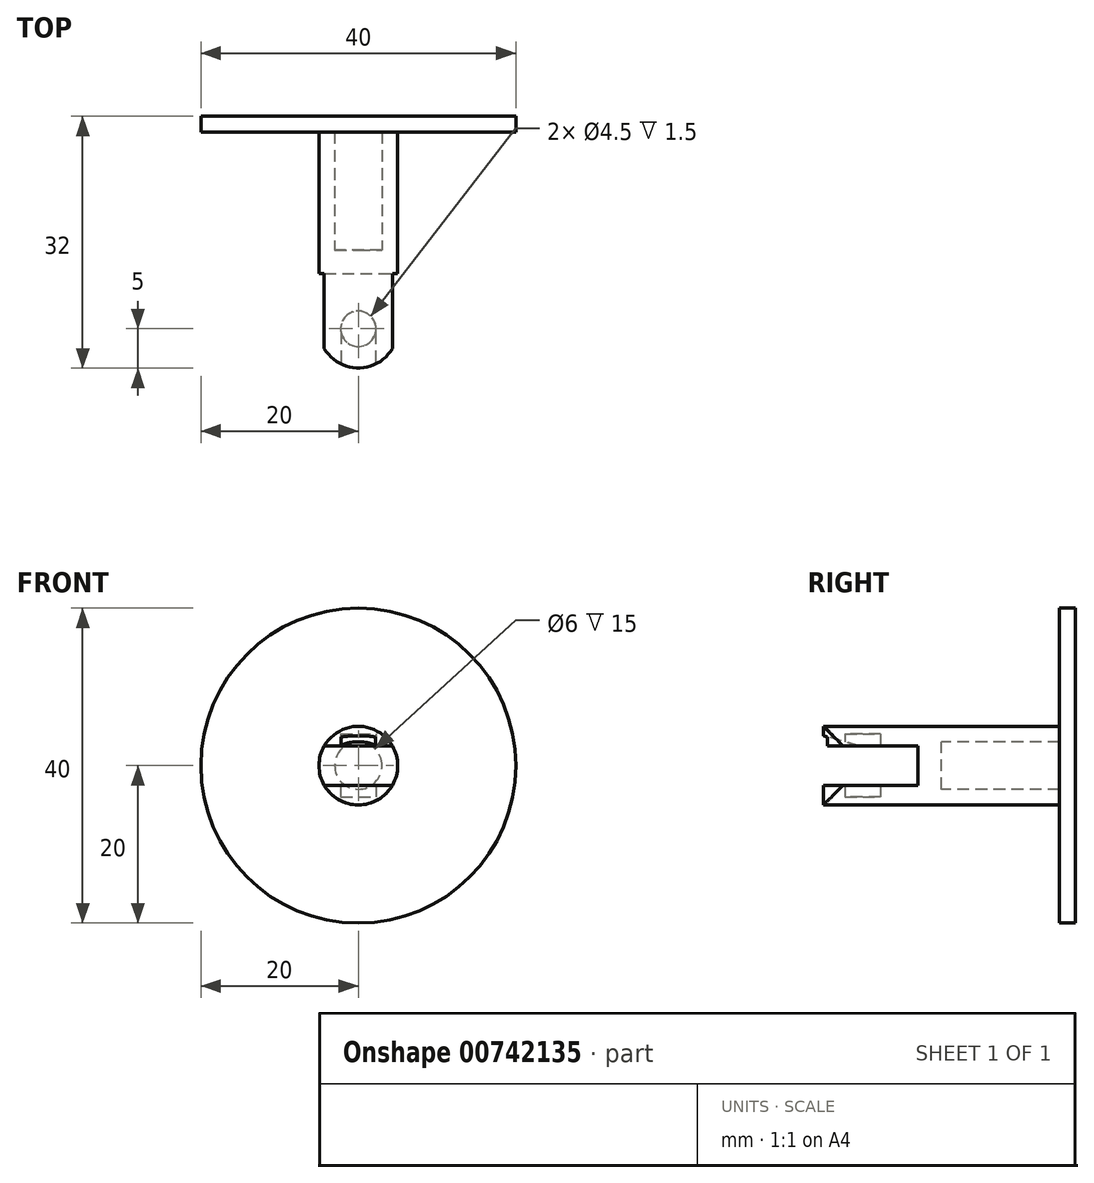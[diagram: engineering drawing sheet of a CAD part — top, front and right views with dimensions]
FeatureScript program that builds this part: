
annotation { "Feature Type Name" : "Feature", "Feature Type Description" : "" }
export const myFeature = defineFeature(function(context is Context, id is Id, definition is map)
    precondition{}
    {
        {
            var Q0;
            Q0=qCreatedBy(makeId("Front.planeOp"),FACE);
            var sketch = newSketch(context, id + "F0", { "sketchPlane" : qUnion([Q0])});
            skCircle(sketch, "E0", {"center": v(0, 0) * mm, "radius": 20 * mm});
            skSolve(sketch);
        }
        {
            var Q0;
            Q0=makeQuery(id+"F0.imprint","IMPRINT",FACE,{"disambiguationData":[TD([[makeQuery(id+"F0.imprint","IMPRINT",EDGE,{"derivedFrom":sQuery(id+"F0.wireOp",EDGE,"E0")}),1.0]])]});
            extrude(context, id + "F1", {"entities" : qUnion([Q0]), "depth" : 2 * mm, "offsetDistance" : 25 * mm});
        }
        {
            var Q0;
            Q0=makeQuery(id+"F1.opExtrude","CAP_FACE",FACE,{"disambiguationData":[OSD([sQuery(id+"F0.wireOp",EDGE,"E0")])],"isStart":false});
            var sketch = newSketch(context, id + "F2", { "sketchPlane" : qUnion([Q0])});
            skCircle(sketch, "E1", {"center": v(0, 0) * mm, "radius": 5 * mm});
            skSolve(sketch);
        }
        {
            var Q0;
            Q0 = qSketchRegion(id + "F2", true);
            extrude(context, id + "F3", {"entities" : qUnion([Q0]), "operationType" : NewBodyOperationType.ADD, "depth" : 30 * mm, "offsetDistance" : 25 * mm});
        }
        {
            var Q0;
            Q0=makeQuery(id+"F3.opExtrude","CAP_FACE",FACE,{"disambiguationData":[OSD([sQuery(id+"F2.wireOp",EDGE,"E1")])],"isStart":false});
            var sketch = newSketch(context, id + "F4", { "sketchPlane" : qUnion([Q0])});
            skSolve(sketch);
        }
        {
            var Q0;
            Q0=makeQuery(id+"F4.imprint","IMPRINT",FACE,{"disambiguationData":[TD([[makeQuery(id+"F4.imprint","IMPRINT",EDGE,{"derivedFrom":makeQuery(id+"F3.opExtrude","CAP_EDGE",EDGE,{"disambiguationData":[OSD([sQuery(id+"F2.wireOp",EDGE,"E1")])],"isStart":false})}),1.0]])]});
            var sketch = newSketch(context, id + "F5", { "sketchPlane" : qUnion([Q0])});
            skLineSegment(sketch, "E2.bottom", {"start": v(-5, 2.5) * mm, "end": v(5, 2.5) * mm});
            skLineSegment(sketch, "E2.top", {"start": v(-5, -2.5) * mm, "end": v(5, -2.5) * mm});
            skLineSegment(sketch, "E2.left", {"start": v(-5, 2.5) * mm, "end": v(-5, -2.5) * mm});
            skLineSegment(sketch, "E2.right", {"start": v(5, 2.5) * mm, "end": v(5, -2.5) * mm});
            skCircle(sketch, "E3.0", {"center": v(0, 0) * mm, "radius": 5 * mm});
            skSolve(sketch);
        }
        {
            var Q0;
            {var subQ0=sQuery(id+"F5.wireOp",EDGE,"E3.0");var subQ1=sQuery(id+"F5.wireOp",EDGE,"E2.bottom");var subQ2=makeQuery(id+"F5.imprint","INTERSECT",VERTEX,{"disambiguationData":[OD(0.0)],"derivedFrom":[subQ1,subQ0]});Q0=makeQuery(id+"F5.imprint","IMPRINT",FACE,{"disambiguationData":[TD([[makeQuery(id+"F5.imprint","IMPRINT",EDGE,{"disambiguationData":[TD([[subQ2,-1.0]])],"derivedFrom":subQ1}),-1.0]])]});}
            extrude(context, id + "F6", {"entities" : qUnion([Q0]), "operationType" : NewBodyOperationType.REMOVE, "oppositeDirection" : true, "depth" : 12 * mm, "offsetDistance" : 25 * mm});
        }
        {
            var Q0;
            Q0=makeQuery(id+"F6.boolean.opBoolean","COPY",FACE,{"derivedFrom":makeQuery(id+"F6.opExtrude","SWEPT_FACE",FACE,{"disambiguationData":[OSD([sQuery(id+"F5.wireOp",EDGE,"E2.bottom")])]})});
            var sketch = newSketch(context, id + "F7", { "sketchPlane" : qUnion([Q0])});
            skCircle(sketch, "E4", {"center": v(0, 27) * mm, "radius": 2.25 * mm});
            skSolve(sketch);
        }
        {
            var Q0;
            Q0 = qSketchRegion(id + "F7", true);
            extrude(context, id + "F8", {"entities" : qUnion([Q0]), "operationType" : NewBodyOperationType.REMOVE, "oppositeDirection" : true, "depth" : 1.5 * mm, "offsetDistance" : 25 * mm, "hasSecondDirection" : true, "secondDirectionOppositeDirection" : false, "secondDirectionDepth" : 6.5 * mm});
        }
        {
            var Q0;
            Q0=makeQuery(id+"F6.boolean.opBoolean","COPY",FACE,{"derivedFrom":makeQuery(id+"F6.opExtrude","SWEPT_FACE",FACE,{"disambiguationData":[OSD([sQuery(id+"F5.wireOp",EDGE,"E2.top")])]})});
            var sketch = newSketch(context, id + "F9", { "sketchPlane" : qUnion([Q0])});
            skCircle(sketch, "E5", {"center": v(0, -27) * mm, "radius": 5 * mm});
            skSolve(sketch);
        }
        {
            var Q0;
            {var subQ0=sQuery(id+"F9.wireOp",EDGE,"E5");var subQ1=sQuery(id+"F5.wireOp",EDGE,"E2.top");var subQ2=makeQuery(id+"F6.boolean.opBoolean","COPY",EDGE,{"derivedFrom":makeQuery(id+"F6.opExtrude","CAP_EDGE",EDGE,{"disambiguationData":[OSD([subQ1])],"isStart":true})});var subQ3=makeQuery(id+"F9.imprint","INTERSECT",VERTEX,{"derivedFrom":[subQ2,subQ0]});Q0=makeQuery(id+"F9.imprint","IMPRINT",FACE,{"disambiguationData":[TD([[makeQuery(id+"F9.imprint","IMPRINT",EDGE,{"disambiguationData":[TD([[subQ3,-1.0]])],"derivedFrom":subQ0}),-1.0]])]});}
            var Q1;
            {var subQ0=sQuery(id+"F9.wireOp",EDGE,"E5");var subQ2=sQuery(id+"F5.wireOp",EDGE,"E2.top");var subQ5=makeQuery(id+"F6.boolean.opBoolean","COPY",EDGE,{"derivedFrom":makeQuery(id+"F6.opExtrude","CAP_EDGE",EDGE,{"disambiguationData":[OSD([subQ2])],"isStart":true})});var subQ6=makeQuery(id+"F9.imprint","INTERSECT",VERTEX,{"derivedFrom":[subQ5,subQ0]});Q1=makeQuery(id+"F9.imprint","IMPRINT",FACE,{"disambiguationData":[TD([[makeQuery(id+"F9.imprint","IMPRINT",EDGE,{"disambiguationData":[TD([[subQ6,1.0]])],"derivedFrom":subQ0}),-1.0]])]});}
            extrude(context, id + "F10", {"entities" : qUnion([Q0, Q1]), "operationType" : NewBodyOperationType.REMOVE, "endBound" : BoundingType.THROUGH_ALL, "oppositeDirection" : true, "depth" : 25 * mm, "offsetDistance" : 25 * mm, "hasSecondDirection" : true, "secondDirectionBound" : SecondDirectionBoundingType.THROUGH_ALL, "secondDirectionOppositeDirection" : false, "secondDirectionDepth" : 25 * mm});
        }
        {
            var Q0;
            Q0=qCreatedBy(makeId("Right.planeOp"),FACE);
            var sketch = newSketch(context, id + "F11", { "sketchPlane" : qUnion([Q0])});
            skLineSegment(sketch, "E6.0.0", {"start": v(-20, 2.5) * mm, "end": v(-29.5, 2.5) * mm});
            skLineSegment(sketch, "E6.0.1", {"start": v(-29.5, 2.5) * mm, "end": v(-32, 2.5) * mm});
            skLineSegment(sketch, "E6.0.2", {"start": v(-29.5, 2.5) * mm, "end": v(-20, 2.5) * mm});
            skLineSegment(sketch, "E7", {"start": v(-32, 2.5) * mm, "end": v(-32, 5) * mm});
            skLineSegment(sketch, "E8", {"start": v(-32, 5) * mm, "end": v(-2, 5) * mm});
            skLineSegment(sketch, "E9.0.0", {"start": v(-29.5, -2.5) * mm, "end": v(-32, -2.5) * mm});
            skLineSegment(sketch, "E9.0.1", {"start": v(-29.5, -2.5) * mm, "end": v(-20, -2.5) * mm});
            skLineSegment(sketch, "E9.0.3", {"start": v(-20, -2.5) * mm, "end": v(-29.5, -2.5) * mm});
            skLineSegment(sketch, "E10", {"start": v(-32, -5) * mm, "end": v(-32, -2.5) * mm});
            skLineSegment(sketch, "E11", {"start": v(-2, -5) * mm, "end": v(-32, -5) * mm});
            skLineSegment(sketch, "E12.0.0", {"start": v(-20, 2.5) * mm, "end": v(-20, -2.5) * mm});
            skLineSegment(sketch, "E12.0.2", {"start": v(-20, -2.5) * mm, "end": v(-20, 2.5) * mm});
            skLineSegment(sketch, "E13.0", {"start": v(-24.75, 4) * mm, "end": v(-29.25, 4) * mm});
            skLineSegment(sketch, "E14", {"start": v(-29.25, 4) * mm, "end": v(-29.5, 2.5) * mm});
            skLineSegment(sketch, "E15", {"start": v(-29.4, 3.06) * mm, "end": v(-32, 3.8) * mm});
            skLineSegment(sketch, "E16", {"start": v(-29.4, 3.06) * mm, "end": v(-27.47, 2.5) * mm});
            skSolve(sketch);
        }
        {
            var Q0;
            {var subQ0=sQuery(id+"F11.wireOp",EDGE,"E6.0.1");Q0=makeQuery(id+"F11.imprint","IMPRINT",FACE,{"disambiguationData":[TD([[makeQuery(id+"F11.imprint","IMPRINT",EDGE,{"derivedFrom":subQ0}),-1.0]])]});}
            var Q1;
            {var subQ3=sQuery(id+"F11.wireOp",EDGE,"E16");Q1=makeQuery(id+"F11.imprint","IMPRINT",FACE,{"disambiguationData":[TD([[makeQuery(id+"F11.imprint","IMPRINT",EDGE,{"derivedFrom":subQ3}),-1.0]])]});}
            extrude(context, id + "F12", {"entities" : qUnion([Q0, Q1]), "operationType" : NewBodyOperationType.REMOVE, "oppositeDirection" : true, "depth" : 2.2 * mm, "offsetDistance" : 25 * mm, "hasSecondDirection" : true, "secondDirectionOppositeDirection" : false, "secondDirectionDepth" : 2.2 * mm});
        }
        {
            var Q0;
            Q0=makeQuery(id+"F6.boolean.opBoolean","COPY",FACE,{"derivedFrom":makeQuery(id+"F6.opExtrude","SWEPT_FACE",FACE,{"disambiguationData":[OSD([sQuery(id+"F5.wireOp",EDGE,"E2.top")])]})});
            var Q1;
            Q1=makeQuery(id+"F6.boolean.opBoolean","COPY",FACE,{"derivedFrom":makeQuery(id+"F6.opExtrude","SWEPT_FACE",FACE,{"disambiguationData":[OSD([sQuery(id+"F5.wireOp",EDGE,"E2.bottom")])]})});
            cPlane(context, id + "F13", {"entities" : qUnion([Q0, Q1]), "cplaneType" : CPlaneType.MID_PLANE, "offset" : 25 * mm, "width" : 150 * mm, "height" : 150 * mm});
        }
        {
            var Q0;
            Q0=makeQuery(id+"F6.boolean.opBoolean","COPY",FACE,{"derivedFrom":makeQuery(id+"F6.opExtrude","CAP_FACE",FACE,{"disambiguationData":[OSD([sQuery(id+"F5.wireOp",EDGE,"E2.bottom"),sQuery(id+"F5.wireOp",EDGE,"E2.top"),sQuery(id+"F5.wireOp",EDGE,"E3.0")])],"isStart":false})});
            cPlane(context, id + "F14", {"entities" : qUnion([Q0]), "cplaneType" : CPlaneType.OFFSET, "offset" : 3 * mm, "oppositeDirection" : true, "width" : 150 * mm, "height" : 150 * mm});
        }
        {
            var Q0;
            Q0=qCreatedBy(id+"F14.planeOp",FACE);
            var sketch = newSketch(context, id + "F15", { "sketchPlane" : qUnion([Q0])});
            skCircle(sketch, "E17", {"center": v(0, 0) * mm, "radius": 3 * mm});
            skSolve(sketch);
        }
        {
            var Q0;
            Q0 = qSketchRegion(id + "F15", true);
            var Q1;
            Q1=makeQuery(id+"F1.opExtrude","CAP_FACE",FACE,{"disambiguationData":[OSD([sQuery(id+"F0.wireOp",EDGE,"E0")])],"isStart":false});
            extrude(context, id + "F16", {"entities" : qUnion([Q0]), "operationType" : NewBodyOperationType.REMOVE, "endBound" : BoundingType.UP_TO_SURFACE, "oppositeDirection" : true, "depth" : 25 * mm, "endBoundEntityFace" : qUnion([Q1]), "offsetDistance" : 25 * mm});
        }
    });
